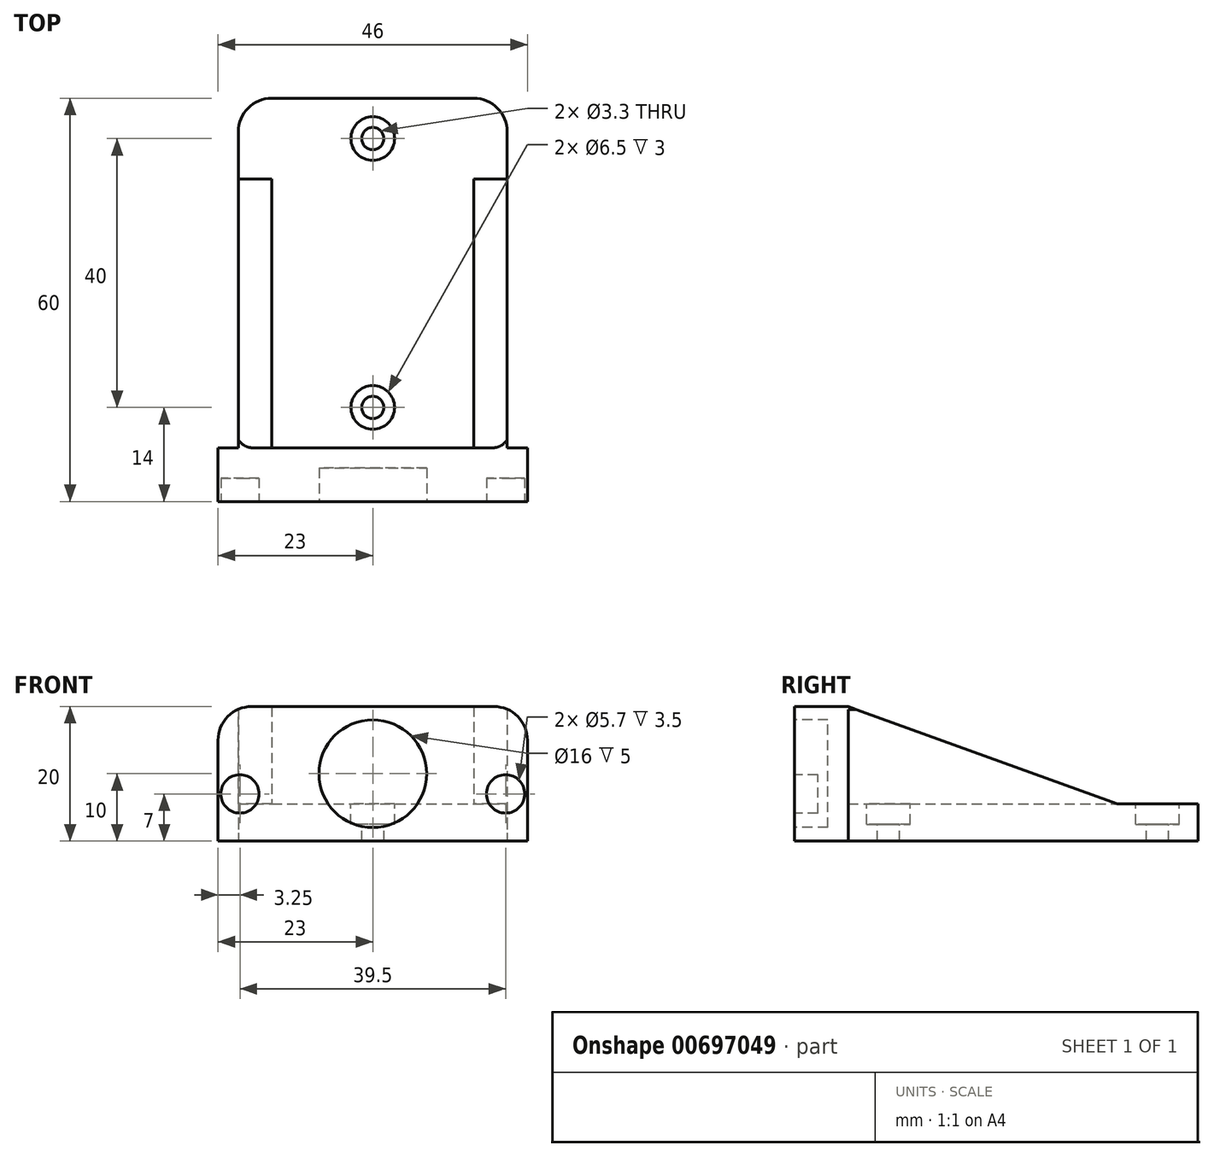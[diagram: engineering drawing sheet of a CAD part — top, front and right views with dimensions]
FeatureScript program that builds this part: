
annotation { "Feature Type Name" : "Feature", "Feature Type Description" : "" }
export const myFeature = defineFeature(function(context is Context, id is Id, definition is map)
    precondition{}
    {
        {
            var Q0;
            Q0=qCreatedBy(makeId("Top.planeOp"),FACE);
            var sketch = newSketch(context, id + "F0", { "sketchPlane" : qUnion([Q0])});
            skLineSegment(sketch, "E0.bottom", {"start": v(20, 30) * mm, "end": v(-20, 30) * mm});
            skLineSegment(sketch, "E0.top", {"start": v(20, -30) * mm, "end": v(-20, -30) * mm});
            skLineSegment(sketch, "E0.left", {"start": v(20, 30) * mm, "end": v(20, -30) * mm});
            skLineSegment(sketch, "E0.right", {"start": v(-20, 30) * mm, "end": v(-20, -30) * mm});
            skPoint(sketch, "E0.middle", {"position": v(0, 0) * mm});
            skLineSegment(sketch, "E1", {"start": v(-20, -22) * mm, "end": v(20, -22) * mm});
            skLineSegment(sketch, "E2", {"start": v(-15, 30) * mm, "end": v(-15, -22) * mm});
            skLineSegment(sketch, "E3.MirrorCS", {"start": v(15, 30) * mm, "end": v(15, -22) * mm});
            skLineSegment(sketch, "E4", {"start": v(20, 18) * mm, "end": v(-20, 18) * mm});
            skLineSegment(sketch, "E5", {"start": v(23, -22) * mm, "end": v(23, -30) * mm});
            skLineSegment(sketch, "E6", {"start": v(23, -22) * mm, "end": v(20, -22) * mm});
            skLineSegment(sketch, "E7", {"start": v(23, -30) * mm, "end": v(20, -30) * mm});
            skLineSegment(sketch, "E8.MirrorCS", {"start": v(-23, -22) * mm, "end": v(-20, -22) * mm});
            skLineSegment(sketch, "E9.MirrorCS", {"start": v(-23, -22) * mm, "end": v(-23, -30) * mm});
            skLineSegment(sketch, "E10.MirrorCS", {"start": v(-23, -30) * mm, "end": v(-20, -30) * mm});
            skSolve(sketch);
        }
        {
            var Q0;
            {var subQ1=sQuery(id+"F0.wireOp",EDGE,"E0.top");Q0=makeQuery(id+"F0.imprint","IMPRINT",FACE,{"disambiguationData":[TD([[makeQuery(id+"F0.imprint","IMPRINT",EDGE,{"derivedFrom":subQ1}),-1.0]])]});}
            var Q1;
            {var subQ2=sQuery(id+"F0.wireOp",EDGE,"E8.MirrorCS");Q1=makeQuery(id+"F0.imprint","IMPRINT",FACE,{"disambiguationData":[TD([[makeQuery(id+"F0.imprint","IMPRINT",EDGE,{"derivedFrom":subQ2}),-1.0]])]});}
            var Q2;
            Q2=makeQuery(id+"F0.imprint","IMPRINT",FACE,{"disambiguationData":[TD([[makeQuery(id+"F0.imprint","IMPRINT",EDGE,{"derivedFrom":sQuery(id+"F0.wireOp",EDGE,"E5")}),-1.0]])]});
            extrude(context, id + "F1", {"entities" : qUnion([Q0, Q1, Q2]), "depth" : 20 * mm, "offsetDistance" : 25 * mm});
        }
        {
            var Q0;
            {var subQ0=sQuery(id+"F0.wireOp",EDGE,"E2");Q0=makeQuery(id+"F0.imprint","IMPRINT",FACE,{"disambiguationData":[TD([[makeQuery(id+"F0.imprint","IMPRINT",EDGE,{"derivedFrom":subQ0}),1.0]])]});}
            var Q1;
            {var subQ3=sQuery(id+"F0.wireOp",EDGE,"E2");Q1=makeQuery(id+"F0.imprint","IMPRINT",FACE,{"disambiguationData":[TD([[makeQuery(id+"F0.imprint","IMPRINT",EDGE,{"derivedFrom":subQ3}),-1.0]])]});}
            var Q2;
            {var subQ3=sQuery(id+"F0.wireOp",EDGE,"E3.MirrorCS");Q2=makeQuery(id+"F0.imprint","IMPRINT",FACE,{"disambiguationData":[TD([[makeQuery(id+"F0.imprint","IMPRINT",EDGE,{"derivedFrom":subQ3}),1.0]])]});}
            extrude(context, id + "F2", {"entities" : qUnion([Q0, Q1, Q2]), "operationType" : NewBodyOperationType.ADD, "depth" : 5.5 * mm, "offsetDistance" : 25 * mm});
        }
        {
            var Q0;
            {var subQ0=sQuery(id+"F0.wireOp",EDGE,"E1");var subQ1=sQuery(id+"F0.wireOp",EDGE,"E0.right");var subQ2=makeQuery(id+"F0.imprint","INTERSECT",VERTEX,{"derivedFrom":[subQ1,subQ0]});Q0=makeQuery(id+"F0.imprint","IMPRINT",FACE,{"disambiguationData":[TD([[makeQuery(id+"F0.imprint","IMPRINT",EDGE,{"disambiguationData":[TD([[subQ2,1.0]])],"derivedFrom":subQ1}),1.0]])]});}
            var Q1;
            {var subQ0=sQuery(id+"F0.wireOp",EDGE,"E1");var subQ1=sQuery(id+"F0.wireOp",EDGE,"E0.left");var subQ2=makeQuery(id+"F0.imprint","INTERSECT",VERTEX,{"derivedFrom":[subQ1,subQ0]});Q1=makeQuery(id+"F0.imprint","IMPRINT",FACE,{"disambiguationData":[TD([[makeQuery(id+"F0.imprint","IMPRINT",EDGE,{"disambiguationData":[TD([[subQ2,1.0]])],"derivedFrom":subQ1}),-1.0]])]});}
            extrude(context, id + "F3", {"entities" : qUnion([Q0, Q1]), "operationType" : NewBodyOperationType.ADD, "depth" : 20 * mm, "offsetDistance" : 25 * mm});
        }
        {
            var Q0;
            {var subQ0=sQuery(id+"F0.wireOp",EDGE,"E0.right");Q0=makeQuery(id+"F3.boolean.opBoolean","MERGE",FACE,{"derivedFrom":[makeQuery(id+"F2.opExtrude","SWEPT_FACE",FACE,{"disambiguationData":[OSD([subQ0])]}),makeQuery(id+"F3.opExtrude","SWEPT_FACE",FACE,{"disambiguationData":[OSD([subQ0])]})]});}
            var sketch = newSketch(context, id + "F4", { "sketchPlane" : qUnion([Q0])});
            skLineSegment(sketch, "E11", {"start": v(-18, 5.5) * mm, "end": v(22, 20) * mm});
            skSolve(sketch);
        }
        {
            var Q0;
            Q0=makeQuery(id+"F4.imprint","IMPRINT",FACE,{"disambiguationData":[TD([[makeQuery(id+"F4.imprint","IMPRINT",EDGE,{"derivedFrom":sQuery(id+"F4.wireOp",EDGE,"E11")}),1.0]])]});
            var Q1;
            {var subQ0=sQuery(id+"F0.wireOp",EDGE,"E0.right");Q1=makeQuery(id+"F3.boolean.opBoolean","MERGE",FACE,{"derivedFrom":[makeQuery(id+"F2.boolean.opBoolean","MERGE",FACE,{"derivedFrom":[makeQuery(id+"F1.opExtrude","SWEPT_FACE",FACE,{"disambiguationData":[OSD([subQ0])]}),makeQuery(id+"F2.opExtrude","SWEPT_FACE",FACE,{"disambiguationData":[OSD([subQ0])]})]}),makeQuery(id+"F3.opExtrude","SWEPT_FACE",FACE,{"disambiguationData":[OSD([subQ0])]})]});}
            extrude(context, id + "F5", {"entities" : qUnion([Q0]), "operationType" : NewBodyOperationType.REMOVE, "endBound" : BoundingType.THROUGH_ALL, "oppositeDirection" : true, "depth" : 25 * mm, "endBoundEntityFace" : qUnion([Q1]), "offsetDistance" : 25 * mm});
        }
        {
            var Q0;
            Q0=makeQuery(id+"F2.opExtrude","CAP_FACE",FACE,{"disambiguationData":[OSD([sQuery(id+"F0.wireOp",EDGE,"E0.bottom"),sQuery(id+"F0.wireOp",EDGE,"E0.left"),sQuery(id+"F0.wireOp",EDGE,"E0.right"),sQuery(id+"F0.wireOp",EDGE,"E1")])],"isStart":false});
            var sketch = newSketch(context, id + "F6", { "sketchPlane" : qUnion([Q0])});
            skLineSegment(sketch, "E12", {"start": v(0, 24) * mm, "end": v(0, -16) * mm});
            skSolve(sketch);
        }
        {
            var Q0;
            Q0=sQuery(id+"F6.wireOp",VERTEX,"E12.start");
            var Q1;
            Q1=sQuery(id+"F6.wireOp",VERTEX,"E12.end");
            var Q2;
            Q2=makeQuery(id+"F1.opExtrude","SWEPT_BODY",BODY,{"disambiguationData":[OSD([sQuery(id+"F0.wireOp",EDGE,"E0.top"),sQuery(id+"F0.wireOp",EDGE,"E0.left"),sQuery(id+"F0.wireOp",EDGE,"E0.right"),sQuery(id+"F0.wireOp",EDGE,"E1")])]});
            hole(context, id + "F7", {"style" : HoleStyle.C_BORE, "endStyle" : HoleEndStyle.BLIND, "standardTappedOrClearance" : lookupTablePath({ "standard" : "ISO", "fit" : "Normal", "size" : "M3", "type" : "Clearance" }), "standardBlindInLast" : lookupTablePath({ "fit" : "Standard", "standard" : "ISO", "size" : "M3", "type" : "Clearance" }), "holeDiameter" : 3.3 * mm, "cBoreDiameter" : 6.5 * mm, "cBoreDepth" : 3 * mm, "majorDiameter" : 3 * mm, "holeDepth" : 13.5 * mm, "isTappedThrough" : true, "tappedDepth" : 12 * mm, "tapClearance" : 3, "locations" : qUnion([Q0, Q1]), "scope" : qUnion([Q2])});
        }
        {
            var Q0;
            Q0=makeQuery(id+"F1.opExtrude","SWEPT_FACE",FACE,{"disambiguationData":[OSD([sQuery(id+"F0.wireOp",EDGE,"E0.top")])]});
            var sketch = newSketch(context, id + "F8", { "sketchPlane" : qUnion([Q0])});
            skLineSegment(sketch, "E13", {"start": v(-19.75, 7) * mm, "end": v(19.75, 7) * mm, "construction": true});
            skCircle(sketch, "E14", {"center": v(0, 10) * mm, "radius": 8 * mm});
            skLineSegment(sketch, "E15", {"start": v(0, 0) * mm, "end": v(0, 7) * mm, "construction": true});
            skCircle(sketch, "E16", {"center": v(19.75, 7) * mm, "radius": 2.85 * mm});
            skCircle(sketch, "E17", {"center": v(-19.75, 7) * mm, "radius": 2.85 * mm});
            skSolve(sketch);
        }
        {
            var Q0;
            Q0=makeQuery(id+"F8.imprint","IMPRINT",FACE,{"disambiguationData":[TD([[makeQuery(id+"F8.imprint","IMPRINT",EDGE,{"derivedFrom":sQuery(id+"F8.wireOp",EDGE,"E14")}),1.0]])]});
            extrude(context, id + "F9", {"entities" : qUnion([Q0]), "operationType" : NewBodyOperationType.REMOVE, "oppositeDirection" : true, "depth" : 5 * mm, "offsetDistance" : 25 * mm});
        }
        {
            var Q0;
            Q0=makeQuery(id+"F8.imprint","IMPRINT",FACE,{"disambiguationData":[TD([[makeQuery(id+"F8.imprint","IMPRINT",EDGE,{"derivedFrom":sQuery(id+"F8.wireOp",EDGE,"E17")}),1.0]])]});
            var Q1;
            Q1=makeQuery(id+"F8.imprint","IMPRINT",FACE,{"disambiguationData":[TD([[makeQuery(id+"F8.imprint","IMPRINT",EDGE,{"derivedFrom":sQuery(id+"F8.wireOp",EDGE,"E16")}),1.0]])]});
            extrude(context, id + "F10", {"entities" : qUnion([Q0, Q1]), "operationType" : NewBodyOperationType.REMOVE, "oppositeDirection" : true, "depth" : 3.5 * mm, "offsetDistance" : 25 * mm});
        }
        {
            var Q0;
            Q0=makeQuery(id+"F2.opExtrude","SWEPT_EDGE",EDGE,{"disambiguationData":[OSD([sQuery(id+"F0.wireOp",EDGE,"E0.bottom"),sQuery(id+"F0.wireOp",EDGE,"E0.left")])]});
            var Q1;
            Q1=makeQuery(id+"F2.opExtrude","SWEPT_EDGE",EDGE,{"disambiguationData":[OSD([sQuery(id+"F0.wireOp",EDGE,"E0.bottom"),sQuery(id+"F0.wireOp",EDGE,"E0.right")])]});
            var Q2;
            Q2=makeQuery(id+"F1.opExtrude","CAP_EDGE",EDGE,{"disambiguationData":[OSD([sQuery(id+"F0.wireOp",EDGE,"E9.MirrorCS")])],"isStart":false});
            var Q3;
            Q3=makeQuery(id+"F1.opExtrude","CAP_EDGE",EDGE,{"disambiguationData":[OSD([sQuery(id+"F0.wireOp",EDGE,"E5")])],"isStart":false});
            fillet(context, id + "F11", {"entities" : qUnion([Q0, Q1, Q2, Q3]), "radius" : 5 * mm, "tangentPropagation" : true, "allowEdgeOverflow" : false});
        }
    });
